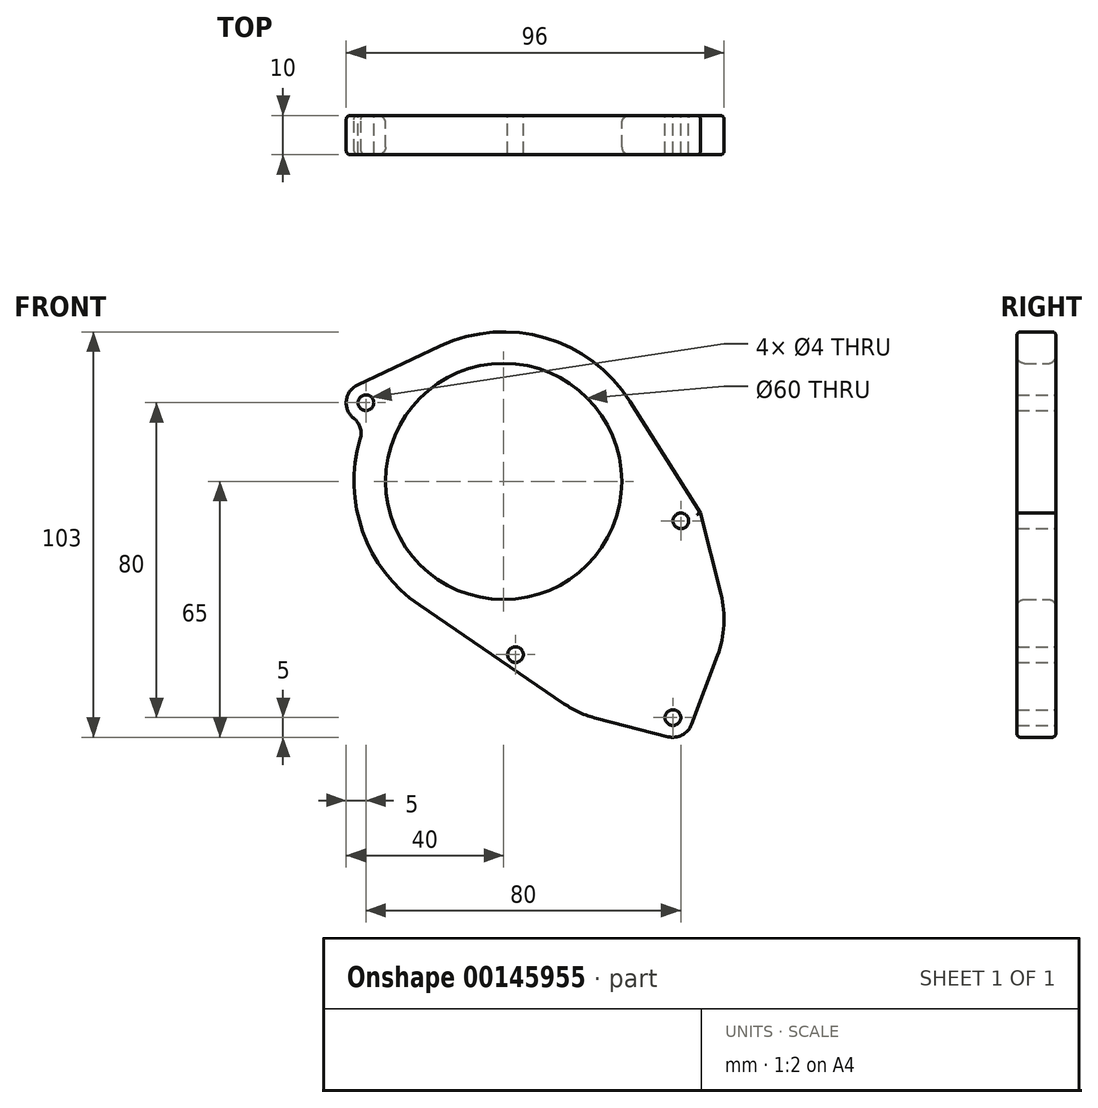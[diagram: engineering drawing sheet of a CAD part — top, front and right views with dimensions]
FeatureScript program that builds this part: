
annotation { "Feature Type Name" : "Feature", "Feature Type Description" : "" }
export const myFeature = defineFeature(function(context is Context, id is Id, definition is map)
    precondition{}
    {
        {
            var Q0;
            Q0=qCreatedBy(makeId("Front.planeOp"),FACE);
            var sketch = newSketch(context, id + "F0", { "sketchPlane" : qUnion([Q0])});
            skArc(sketch, "E0", {"start": v(32.13, 20.3) * mm, "mid": v(10.64, 36.48) * mm, "end": v(-16.18, 34.38) * mm});
            skCircle(sketch, "E1", {"center": v(0, 0) * mm, "radius": 30 * mm});
            skArc(sketch, "E2", {"start": v(15.34, -56.48) * mm, "mid": v(19.29, -58.7) * mm, "end": v(23.56, -60.19) * mm});
            skCircle(sketch, "E3", {"center": v(45, -10) * mm, "radius": 2 * mm});
            skCircle(sketch, "E4", {"center": v(-35, 20) * mm, "radius": 2 * mm});
            skCircle(sketch, "E5", {"center": v(43, -60) * mm, "radius": 2 * mm});
            skCircle(sketch, "E6", {"center": v(3, -44) * mm, "radius": 2 * mm});
            skLineSegment(sketch, "E7", {"start": v(-21.42, -31.39) * mm, "end": v(15.34, -56.48) * mm});
            skLineSegment(sketch, "E8", {"start": v(32.13, 20.3) * mm, "end": v(50, -8) * mm});
            skLineSegment(sketch, "E9", {"start": v(50, -8) * mm, "end": v(55.2, -28.64) * mm});
            skLineSegment(sketch, "E10", {"start": v(42.28, 0) * mm, "end": v(65.3, 0) * mm, "construction": true});
            skArc(sketch, "E11", {"start": v(-37.13, 24.52) * mm, "mid": v(-39.97, 20.58) * mm, "end": v(-38.12, 16.1) * mm});
            skArc(sketch, "E12", {"start": v(41.76, -64.84) * mm, "mid": v(45.3, -64.44) * mm, "end": v(47.68, -61.77) * mm});
            skLineSegment(sketch, "E13", {"start": v(54.32, -44.2) * mm, "end": v(47.68, -61.77) * mm});
            skLineSegment(sketch, "E14", {"start": v(23.56, -60.19) * mm, "end": v(41.76, -64.84) * mm});
            skArc(sketch, "E15.trimOffspring", {"start": v(54.32, -44.2) * mm, "mid": v(55.96, -36.48) * mm, "end": v(55.2, -28.64) * mm});
            skLineSegment(sketch, "E16", {"start": v(-37.13, 24.52) * mm, "end": v(-16.18, 34.38) * mm});
            skArc(sketch, "E17.trimOffspring", {"start": v(-36.44, 10.77) * mm, "mid": v(-35.8, -12.76) * mm, "end": v(-21.42, -31.39) * mm});
            skPoint(sketch, "E18.visualSharp", {"position": v(-34.91, 15) * mm});
            skArc(sketch, "E18.filletArc", {"start": v(-36.44, 10.77) * mm, "mid": v(-36.47, 13.69) * mm, "end": v(-38.12, 16.1) * mm});
            skSolve(sketch);
        }
        {
            var Q0;
            Q0=makeQuery(id+"F0.imprint","IMPRINT",FACE,{"disambiguationData":[TD([[makeQuery(id+"F0.imprint","IMPRINT",EDGE,{"derivedFrom":sQuery(id+"F0.wireOp",EDGE,"E0")}),1.0]])]});
            extrude(context, id + "F1", {"entities" : qUnion([Q0]), "depth" : 10 * mm});
        }
        {
            var Q0;
            Q0=makeQuery(id+"F1.opExtrude","CAP_EDGE",EDGE,{"disambiguationData":[OSD([sQuery(id+"F0.wireOp",EDGE,"E0")])],"isStart":false});
            var Q1;
            Q1=makeQuery(id+"F1.opExtrude","CAP_EDGE",EDGE,{"disambiguationData":[OSD([sQuery(id+"F0.wireOp",EDGE,"E0")])],"isStart":true});
            fillet(context, id + "F2", {"entities" : qUnion([Q0, Q1]), "radius" : 1 * mm, "tangentPropagation" : true, "allowEdgeOverflow" : false});
        }
        {
            var Q0;
            Q0=makeQuery(id+"F1.opExtrude","CAP_EDGE",EDGE,{"disambiguationData":[OSD([sQuery(id+"F0.wireOp",EDGE,"E1")])],"isStart":false});
            var Q1;
            Q1=makeQuery(id+"F1.opExtrude","CAP_EDGE",EDGE,{"disambiguationData":[OSD([sQuery(id+"F0.wireOp",EDGE,"E1")])],"isStart":true});
            fillet(context, id + "F3", {"entities" : qUnion([Q0, Q1]), "radius" : 2 * mm, "tangentPropagation" : true, "allowEdgeOverflow" : false});
        }
        {
            var Q0;
            Q0=makeQuery(id+"F1.opExtrude","CAP_EDGE",EDGE,{"disambiguationData":[OSD([sQuery(id+"F0.wireOp",EDGE,"E4")])],"isStart":true});
            var Q1;
            Q1=makeQuery(id+"F1.opExtrude","CAP_EDGE",EDGE,{"disambiguationData":[OSD([sQuery(id+"F0.wireOp",EDGE,"E6")])],"isStart":true});
            var Q2;
            Q2=makeQuery(id+"F1.opExtrude","CAP_EDGE",EDGE,{"disambiguationData":[OSD([sQuery(id+"F0.wireOp",EDGE,"E3")])],"isStart":true});
            var Q3;
            Q3=makeQuery(id+"F1.opExtrude","CAP_EDGE",EDGE,{"disambiguationData":[OSD([sQuery(id+"F0.wireOp",EDGE,"E5")])],"isStart":true});
            var Q4;
            Q4=makeQuery(id+"F1.opExtrude","CAP_EDGE",EDGE,{"disambiguationData":[OSD([sQuery(id+"F0.wireOp",EDGE,"E4")])],"isStart":false});
            var Q5;
            Q5=makeQuery(id+"F1.opExtrude","CAP_EDGE",EDGE,{"disambiguationData":[OSD([sQuery(id+"F0.wireOp",EDGE,"E6")])],"isStart":false});
            var Q6;
            Q6=makeQuery(id+"F1.opExtrude","CAP_EDGE",EDGE,{"disambiguationData":[OSD([sQuery(id+"F0.wireOp",EDGE,"E3")])],"isStart":false});
            var Q7;
            Q7=makeQuery(id+"F1.opExtrude","CAP_EDGE",EDGE,{"disambiguationData":[OSD([sQuery(id+"F0.wireOp",EDGE,"E5")])],"isStart":false});
            fillet(context, id + "F4", {"entities" : qUnion([Q0, Q1, Q2, Q3, Q4, Q5, Q6, Q7]), "radius" : .3 * mm, "tangentPropagation" : true, "allowEdgeOverflow" : false});
        }
    });
